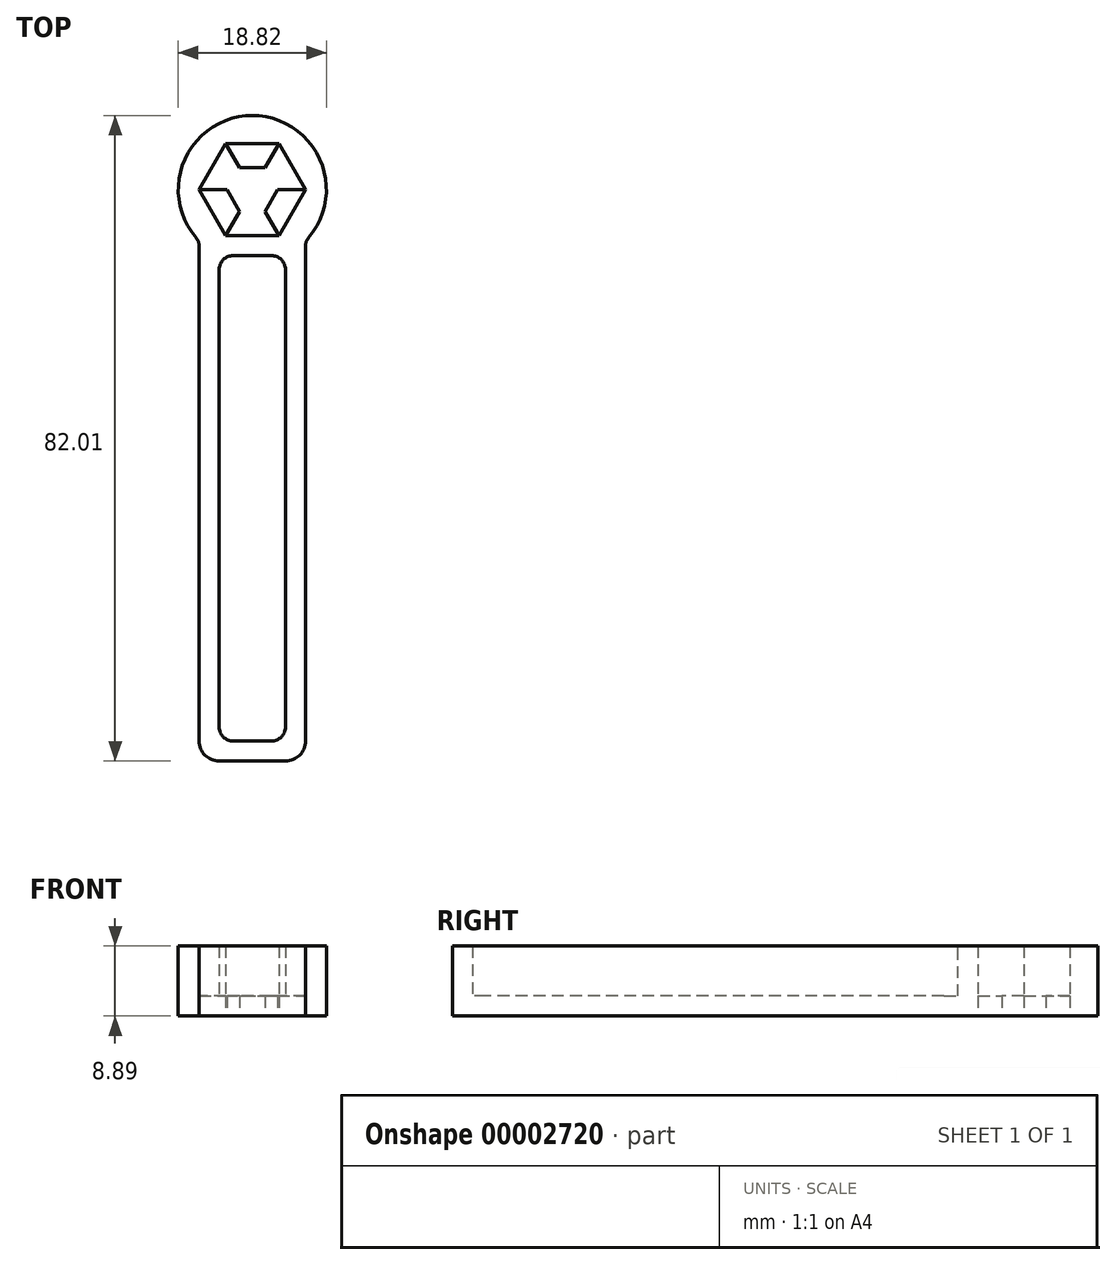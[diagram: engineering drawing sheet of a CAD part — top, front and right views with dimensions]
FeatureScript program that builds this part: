
annotation { "Feature Type Name" : "Feature", "Feature Type Description" : "" }
export const myFeature = defineFeature(function(context is Context, id is Id, definition is map)
    precondition{}
    {
        {
            var Q0;
            Q0=qCreatedBy(makeId("Top.planeOp"),FACE);
            var sketch = newSketch(context, id + "F0", { "sketchPlane" : qUnion([Q0])});
            skCircle(sketch, "E0.cCircle", {"center": v(0, 0) * mm, "radius": 5.84 * mm, "construction": true});
            skLineSegment(sketch, "E0.0", {"start": v(3.37, -5.84) * mm, "end": v(-3.37, -5.84) * mm});
            skLineSegment(sketch, "E0.1", {"start": v(-3.37, -5.84) * mm, "end": v(-6.75, 0) * mm});
            skLineSegment(sketch, "E0.2", {"start": v(-6.75, 0) * mm, "end": v(-3.37, 5.84) * mm});
            skLineSegment(sketch, "E0.3", {"start": v(-3.37, 5.84) * mm, "end": v(3.37, 5.84) * mm});
            skLineSegment(sketch, "E0.4", {"start": v(3.37, 5.84) * mm, "end": v(6.75, 0) * mm});
            skLineSegment(sketch, "E0.5", {"start": v(6.75, 0) * mm, "end": v(3.37, -5.84) * mm});
            skPoint(sketch, "E0.0.midPoint", {"position": v(0, -5.84) * mm});
            skSolve(sketch);
        }
        {
            var Q0;
            Q0=qCreatedBy(makeId("Top.planeOp"),FACE);
            var sketch = newSketch(context, id + "F1", { "sketchPlane" : qUnion([Q0])});
            skArc(sketch, "E1", {"start": v(6.75, -6.56) * mm, "mid": v(0, 9.4) * mm, "end": v(-6.75, -6.56) * mm});
            skLineSegment(sketch, "E2", {"start": v(6.75, -6.56) * mm, "end": v(6.75, -70.06) * mm});
            skLineSegment(sketch, "E3", {"start": v(4.2, -72.6) * mm, "end": v(-4.2, -72.6) * mm});
            skLineSegment(sketch, "E4", {"start": v(-6.75, -70.06) * mm, "end": v(-6.75, -6.56) * mm});
            skPoint(sketch, "E5.orphan", {"position": v(6.75, 0) * mm});
            skPoint(sketch, "E6.orphan", {"position": v(-6.75, 0) * mm});
            skPoint(sketch, "E7.visualSharp", {"position": v(6.75, -72.6) * mm});
            skArc(sketch, "E7.filletArc", {"start": v(4.2, -72.6) * mm, "mid": v(6, -71.86) * mm, "end": v(6.75, -70.06) * mm});
            skPoint(sketch, "E8.visualSharp", {"position": v(-6.75, -72.6) * mm});
            skArc(sketch, "E8.filletArc", {"start": v(-6.75, -70.06) * mm, "mid": v(-6, -71.86) * mm, "end": v(-4.2, -72.6) * mm});
            skSolve(sketch);
        }
        {
            var Q0;
            Q0=makeQuery(id+"F1.imprint","IMPRINT",FACE,{"disambiguationData":[TD([[makeQuery(id+"F1.imprint","IMPRINT",EDGE,{"derivedFrom":sQuery(id+"F1.wireOp",EDGE,"E1")}),1.0]])]});
            extrude(context, id + "F2", {"entities" : qUnion([Q0]), "depth" : 8.9 * mm});
        }
        {
            var Q0;
            Q0=makeQuery(id+"F0.imprint","IMPRINT",FACE,{"disambiguationData":[TD([[makeQuery(id+"F0.imprint","IMPRINT",EDGE,{"derivedFrom":sQuery(id+"F0.wireOp",EDGE,"E0.0")}),-1.0]])]});
            extrude(context, id + "F3", {"entities" : qUnion([Q0]), "operationType" : NewBodyOperationType.REMOVE, "depth" : 25.4 * mm});
        }
        {
            var Q0;
            Q0=qCreatedBy(makeId("Top.planeOp"),FACE);
            var sketch = newSketch(context, id + "F4", { "sketchPlane" : qUnion([Q0])});
            skCircle(sketch, "E9.cCircle", {"center": v(0, 0) * mm, "radius": 2.8 * mm, "construction": true});
            skLineSegment(sketch, "E9.0", {"start": v(1.61, -2.8) * mm, "end": v(-1.61, -2.8) * mm});
            skLineSegment(sketch, "E9.1", {"start": v(-1.61, -2.8) * mm, "end": v(-3.23, 0) * mm});
            skLineSegment(sketch, "E9.2", {"start": v(-3.23, 0) * mm, "end": v(-1.61, 2.8) * mm});
            skLineSegment(sketch, "E9.3", {"start": v(-1.61, 2.8) * mm, "end": v(1.61, 2.8) * mm});
            skLineSegment(sketch, "E9.4", {"start": v(1.61, 2.8) * mm, "end": v(3.23, 0) * mm});
            skLineSegment(sketch, "E9.5", {"start": v(3.23, 0) * mm, "end": v(1.61, -2.8) * mm});
            skPoint(sketch, "E9.0.midPoint", {"position": v(0, -2.8) * mm});
            skLineSegment(sketch, "E10", {"start": v(-1.61, -2.8) * mm, "end": v(-3.37, -5.84) * mm});
            skLineSegment(sketch, "E11", {"start": v(-3.37, -5.84) * mm, "end": v(3.37, -5.84) * mm});
            skLineSegment(sketch, "E12", {"start": v(3.37, -5.84) * mm, "end": v(1.61, -2.8) * mm});
            skLineSegment(sketch, "E13", {"start": v(3.23, 0) * mm, "end": v(6.75, 0) * mm});
            skLineSegment(sketch, "E14", {"start": v(6.75, 0) * mm, "end": v(3.37, 5.84) * mm});
            skLineSegment(sketch, "E15", {"start": v(3.37, 5.84) * mm, "end": v(1.61, 2.8) * mm});
            skLineSegment(sketch, "E16", {"start": v(-1.61, 2.8) * mm, "end": v(-3.37, 5.84) * mm});
            skLineSegment(sketch, "E17", {"start": v(-3.37, 5.84) * mm, "end": v(-6.75, 0) * mm});
            skLineSegment(sketch, "E18", {"start": v(-6.75, 0) * mm, "end": v(-3.23, 0) * mm});
            skSolve(sketch);
        }
        {
            var Q0;
            {var subQ0=makeQuery(id+"F4.imprint","IMPRINT",EDGE,{"derivedFrom":sQuery(id+"F4.wireOp",EDGE,"E9.0")});var subQ1=makeQuery(id+"F4.imprint","IMPRINT",EDGE,{"derivedFrom":sQuery(id+"F4.wireOp",EDGE,"E9.2")});var subQ2=makeQuery(id+"F4.imprint","IMPRINT",EDGE,{"derivedFrom":sQuery(id+"F4.wireOp",EDGE,"E9.4")});Q0=qUnion([makeQuery(id+"F4.imprint","IMPRINT",FACE,{"disambiguationData":[TD([[subQ0,1.0]])]}),makeQuery(id+"F4.imprint","IMPRINT",FACE,{"disambiguationData":[TD([[subQ1,1.0]])]}),makeQuery(id+"F4.imprint","IMPRINT",FACE,{"disambiguationData":[TD([[subQ2,1.0]])]}),makeQuery(id+"F4.imprint","IMPRINT",FACE,{"disambiguationData":[TD([[subQ0,-1.0]])]})]);}
            extrude(context, id + "F5", {"entities" : qUnion([Q0]), "operationType" : NewBodyOperationType.ADD, "depth" : 2.54 * mm});
        }
        {
            var Q0;
            Q0=makeQuery(id+"F2.opExtrude","CAP_FACE",FACE,{"disambiguationData":[OSD([sQuery(id+"F1.wireOp",EDGE,"E1"),sQuery(id+"F1.wireOp",EDGE,"E2"),sQuery(id+"F1.wireOp",EDGE,"E3"),sQuery(id+"F1.wireOp",EDGE,"E4"),sQuery(id+"F1.wireOp",EDGE,"E7.filletArc"),sQuery(id+"F1.wireOp",EDGE,"E8.filletArc")])],"isStart":false});
            shell(context, id + "F6", {"entities" : qUnion([Q0]), "thickness" : 2.54 * mm});
        }
        {
            var Q0;
            Q0=makeQuery(id+"F6.opShell","TWEAK_EDGE",EDGE,{"derivedFrom":[makeQuery(id+"F2.opExtrude","SWEPT_FACE",FACE,{"disambiguationData":[OSD([sQuery(id+"F1.wireOp",EDGE,"E4")])]}),makeQuery(id+"F3.boolean.opBoolean","COPY",FACE,{"derivedFrom":makeQuery(id+"F3.opExtrude","SWEPT_FACE",FACE,{"disambiguationData":[OSD([sQuery(id+"F0.wireOp",EDGE,"E0.0")])]})})]});
            var Q1;
            Q1=makeQuery(id+"F6.opShell","TWEAK_EDGE",EDGE,{"derivedFrom":[makeQuery(id+"F2.opExtrude","SWEPT_FACE",FACE,{"disambiguationData":[OSD([sQuery(id+"F1.wireOp",EDGE,"E2")])]}),makeQuery(id+"F3.boolean.opBoolean","COPY",FACE,{"derivedFrom":makeQuery(id+"F3.opExtrude","SWEPT_FACE",FACE,{"disambiguationData":[OSD([sQuery(id+"F0.wireOp",EDGE,"E0.0")])]})})]});
            var Q2;
            Q2=makeQuery(id+"F6.opShell","OFFSET_EDGE",EDGE,{"disambiguationData":[OSD([sQuery(id+"F1.wireOp",EDGE,"E2"),sQuery(id+"F1.wireOp",EDGE,"E3"),sQuery(id+"F1.wireOp",EDGE,"E7.filletArc")])]});
            var Q3;
            Q3=makeQuery(id+"F6.opShell","OFFSET_EDGE",EDGE,{"disambiguationData":[OSD([sQuery(id+"F1.wireOp",EDGE,"E3"),sQuery(id+"F1.wireOp",EDGE,"E4"),sQuery(id+"F1.wireOp",EDGE,"E8.filletArc")])]});
            var Q4;
            Q4=makeQuery(id+"F2.opExtrude","SWEPT_EDGE",EDGE,{"disambiguationData":[OSD([sQuery(id+"F1.wireOp",EDGE,"E1"),sQuery(id+"F1.wireOp",EDGE,"E2")])]});
            var Q5;
            Q5=makeQuery(id+"F2.opExtrude","SWEPT_EDGE",EDGE,{"disambiguationData":[OSD([sQuery(id+"F1.wireOp",EDGE,"E1"),sQuery(id+"F1.wireOp",EDGE,"E4")])]});
            fillet(context, id + "F7", {"entities" : qUnion([Q0, Q1, Q2, Q3, Q4, Q5]), "radius" : 1.78 * mm, "tangentPropagation" : true, "allowEdgeOverflow" : false});
        }
    });
